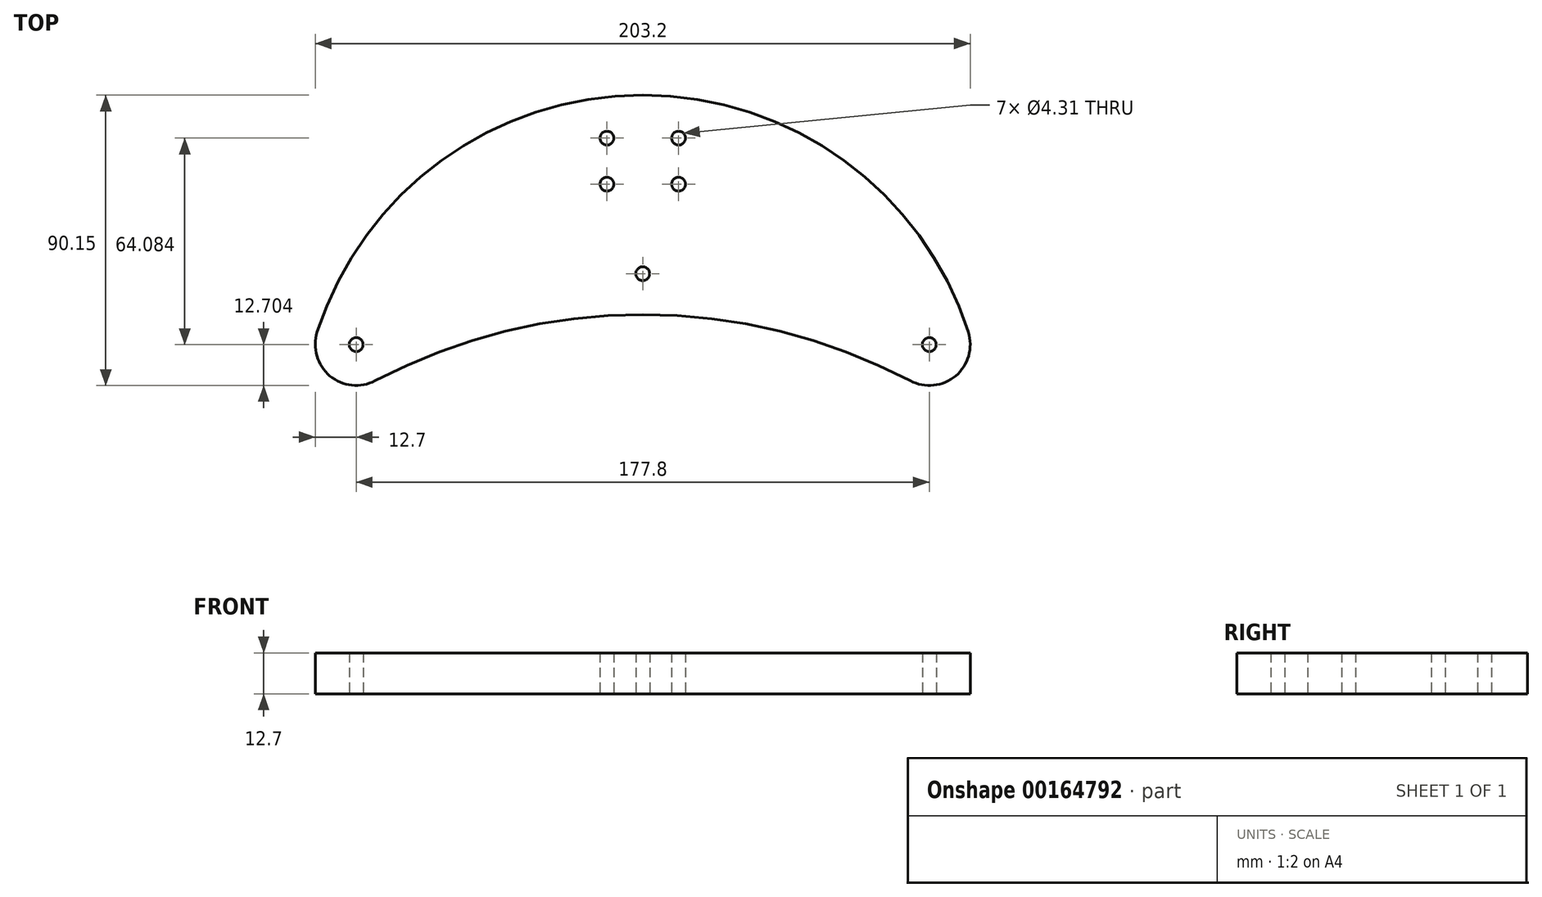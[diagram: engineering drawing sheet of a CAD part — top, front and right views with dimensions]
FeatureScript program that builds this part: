
annotation { "Feature Type Name" : "Feature", "Feature Type Description" : "" }
export const myFeature = defineFeature(function(context is Context, id is Id, definition is map)
    precondition{}
    {
        {
            var Q0;
            Q0=qCreatedBy(makeId("Top.planeOp"),FACE);
            var sketch = newSketch(context, id + "F0", { "sketchPlane" : qUnion([Q0])});
            skLineSegment(sketch, "E0", {"start": v(0, 0) * mm, "end": v(203.2, 0) * mm, "construction": true});
            skLineSegment(sketch, "E1", {"start": v(101.6, 0) * mm, "end": v(101.6, 0) * mm});
            skLineSegment(sketch, "E2", {"start": v(0, 0) * mm, "end": v(0, -254) * mm});
            skLineSegment(sketch, "E3", {"start": v(203.2, 0) * mm, "end": v(203.2, -254) * mm});
            skArc(sketch, "E4", {"start": v(184.57, 4.85) * mm, "mid": v(101.6, 25.4) * mm, "end": v(18.63, 4.85) * mm});
            skLineSegment(sketch, "E5", {"start": v(101.6, 0) * mm, "end": v(101.6, -152.4) * mm, "construction": true});
            skCircle(sketch, "E6", {"center": v(101.6, 38.1) * mm, "radius": 12.7 * mm, "construction": true});
            skCircle(sketch, "E7", {"center": v(12.7, 16.08) * mm, "radius": 2.15 * mm});
            skCircle(sketch, "E8", {"center": v(101.6, 38.1) * mm, "radius": 2.15 * mm});
            skCircle(sketch, "E9", {"center": v(190.5, 16.08) * mm, "radius": 2.15 * mm});
            skLineSegment(sketch, "E10", {"start": v(0, 0) * mm, "end": v(0, 0) * mm});
            skLineSegment(sketch, "E11", {"start": v(203.2, 0) * mm, "end": v(203.2, 0) * mm});
            skArc(sketch, "E12", {"start": v(0.61, 19.98) * mm, "mid": v(4.53, 6.36) * mm, "end": v(18.63, 4.85) * mm});
            skArc(sketch, "E13", {"start": v(184.57, 4.85) * mm, "mid": v(198.67, 6.36) * mm, "end": v(202.59, 19.98) * mm});
            skArc(sketch, "E14", {"start": v(202.59, 19.98) * mm, "mid": v(101.6, 93.53) * mm, "end": v(0.61, 19.98) * mm});
            skLineSegment(sketch, "E15.bottom", {"start": v(112.71, 65.88) * mm, "end": v(90.49, 65.88) * mm, "construction": true});
            skLineSegment(sketch, "E15.top", {"start": v(112.71, 80.17) * mm, "end": v(90.49, 80.17) * mm, "construction": true});
            skLineSegment(sketch, "E15.left", {"start": v(112.71, 65.88) * mm, "end": v(112.71, 80.17) * mm, "construction": true});
            skLineSegment(sketch, "E15.right", {"start": v(90.49, 65.88) * mm, "end": v(90.49, 80.17) * mm, "construction": true});
            skPoint(sketch, "E15.middle", {"position": v(101.6, 73.03) * mm});
            skLineSegment(sketch, "E16", {"start": v(101.6, 38.1) * mm, "end": v(101.6, 0) * mm, "construction": true});
            skLineSegment(sketch, "E17", {"start": v(101.6, 38.1) * mm, "end": v(101.6, 73.03) * mm, "construction": true});
            skCircle(sketch, "E18", {"center": v(90.49, 80.17) * mm, "radius": 12.7 * mm, "construction": true});
            skCircle(sketch, "E19", {"center": v(90.49, 80.17) * mm, "radius": 2.15 * mm});
            skCircle(sketch, "E20", {"center": v(112.71, 80.17) * mm, "radius": 2.15 * mm});
            skCircle(sketch, "E21", {"center": v(112.71, 65.88) * mm, "radius": 2.15 * mm});
            skCircle(sketch, "E22", {"center": v(90.49, 65.88) * mm, "radius": 2.15 * mm});
            skSolve(sketch);
        }
        {
            var Q0;
            Q0=qSketchRegion(id+"F0",true);
            extrude(context, id + "F1", {"entities" : qUnion([Q0]), "depth" : 12.7 * mm});
        }
    });
